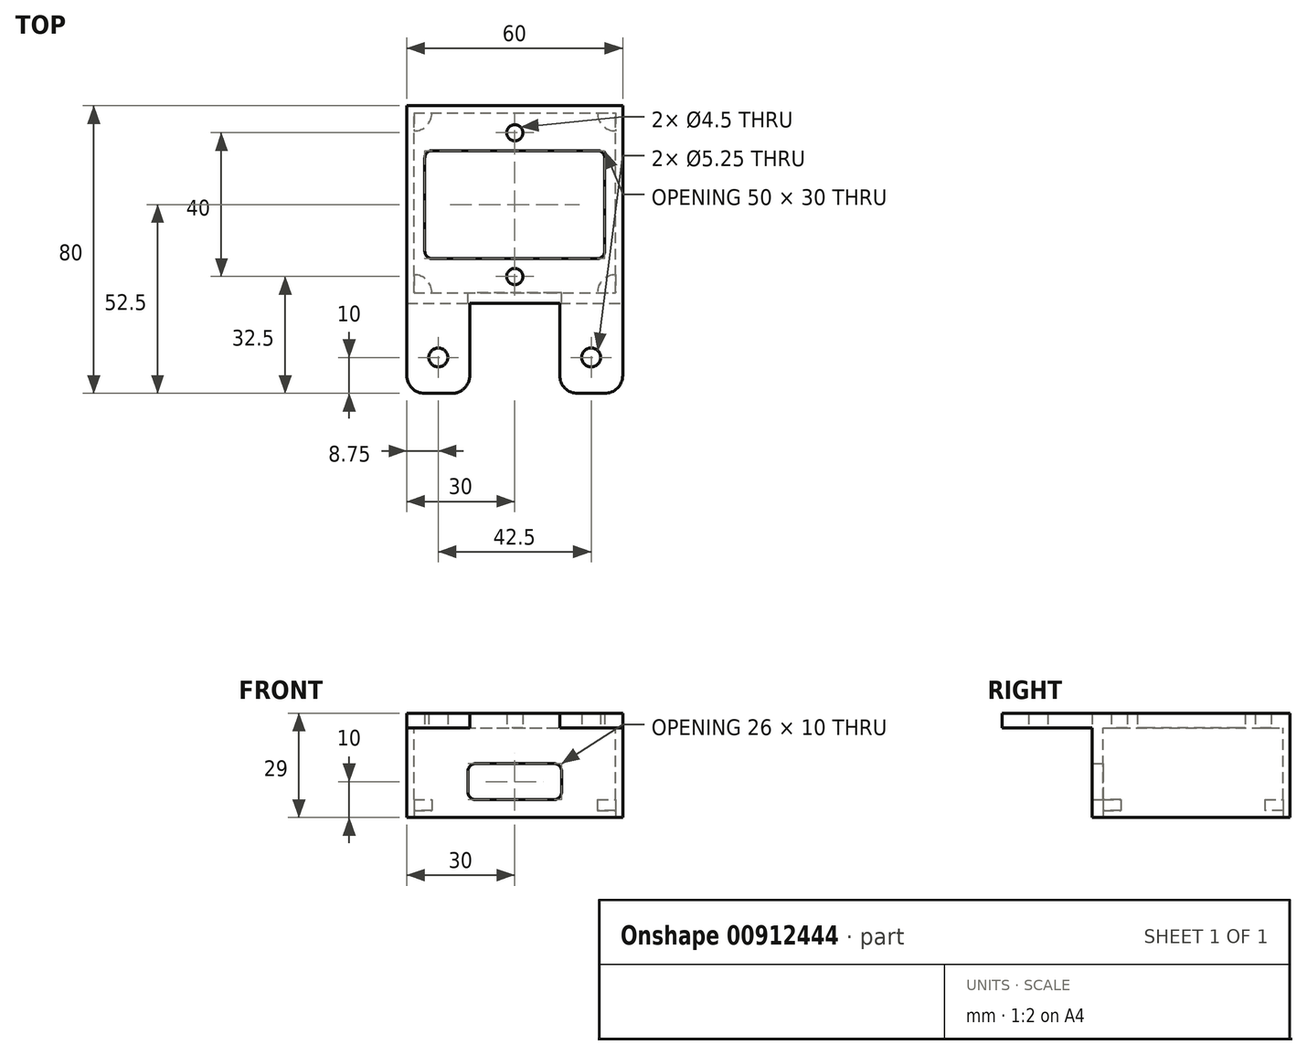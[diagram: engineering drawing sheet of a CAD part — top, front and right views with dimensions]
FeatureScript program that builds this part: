
annotation { "Feature Type Name" : "Feature", "Feature Type Description" : "" }
export const myFeature = defineFeature(function(context is Context, id is Id, definition is map)
    precondition{}
    {
        {
            var Q0;
            Q0=qCreatedBy(makeId("Top.planeOp"),FACE);
            var sketch = newSketch(context, id + "F0", { "sketchPlane" : qUnion([Q0])});
            skLineSegment(sketch, "E0.bottom", {"start": v(-30, 27.5) * mm, "end": v(30, 27.5) * mm});
            skLineSegment(sketch, "E0.left", {"start": v(-30, 27.5) * mm, "end": v(-30, -27.5) * mm});
            skLineSegment(sketch, "E0.right", {"start": v(30, 27.5) * mm, "end": v(30, -27.5) * mm});
            skLineSegment(sketch, "E1.bottom", {"start": v(-23, 15) * mm, "end": v(23, 15) * mm});
            skLineSegment(sketch, "E1.top", {"start": v(-23, -15) * mm, "end": v(23, -15) * mm});
            skLineSegment(sketch, "E1.left", {"start": v(-25, 13) * mm, "end": v(-25, -13) * mm});
            skLineSegment(sketch, "E1.right", {"start": v(25, 13) * mm, "end": v(25, -13) * mm});
            skCircle(sketch, "E2", {"center": v(0, 20) * mm, "radius": 2.25 * mm});
            skCircle(sketch, "E3", {"center": v(0, -20) * mm, "radius": 2.25 * mm});
            skPoint(sketch, "E4.visualSharp", {"position": v(-25, 15) * mm});
            skArc(sketch, "E4.filletArc", {"start": v(-23, 15) * mm, "mid": v(-24.41, 14.41) * mm, "end": v(-25, 13) * mm});
            skPoint(sketch, "E5.visualSharp", {"position": v(-25, -15) * mm});
            skArc(sketch, "E5.filletArc", {"start": v(-25, -13) * mm, "mid": v(-24.41, -14.41) * mm, "end": v(-23, -15) * mm});
            skPoint(sketch, "E6.visualSharp", {"position": v(25, -15) * mm});
            skArc(sketch, "E6.filletArc", {"start": v(23, -15) * mm, "mid": v(24.41, -14.41) * mm, "end": v(25, -13) * mm});
            skPoint(sketch, "E7.visualSharp", {"position": v(25, 15) * mm});
            skArc(sketch, "E7.filletArc", {"start": v(25, 13) * mm, "mid": v(24.41, 14.41) * mm, "end": v(23, 15) * mm});
            skLineSegment(sketch, "E8.top", {"start": v(-25, -52.5) * mm, "end": v(-17.5, -52.5) * mm});
            skLineSegment(sketch, "E8.left", {"start": v(-30, -27.5) * mm, "end": v(-30, -47.5) * mm});
            skLineSegment(sketch, "E9.bottom", {"start": v(30, -27.5) * mm, "end": v(12.5, -27.5) * mm});
            skLineSegment(sketch, "E9.top", {"start": v(25, -52.5) * mm, "end": v(17.5, -52.5) * mm});
            skLineSegment(sketch, "E9.left", {"start": v(30, -27.5) * mm, "end": v(30, -47.5) * mm});
            skLineSegment(sketch, "E9.right", {"start": v(12.5, -27.5) * mm, "end": v(12.5, -47.5) * mm});
            skCircle(sketch, "E10", {"center": v(-21.25, -42.5) * mm, "radius": 2.62 * mm});
            skCircle(sketch, "E11", {"center": v(21.25, -42.5) * mm, "radius": 2.62 * mm});
            skPoint(sketch, "E12.visualSharp", {"position": v(-30, -52.5) * mm});
            skPoint(sketch, "E13.visualSharp", {"position": v(-12.5, -52.5) * mm});
            skPoint(sketch, "E14.visualSharp", {"position": v(12.5, -52.5) * mm});
            skPoint(sketch, "E15.visualSharp", {"position": v(30, -52.5) * mm});
            skArc(sketch, "E15.filletArc", {"start": v(25, -52.5) * mm, "mid": v(28.54, -51.04) * mm, "end": v(30, -47.5) * mm});
            skPoint(sketch, "E16.visualSharp", {"position": v(30, 27.5) * mm});
            skPoint(sketch, "E17.visualSharp", {"position": v(-30, 27.5) * mm});
            skLineSegment(sketch, "E18.filletArc", {"start": v(-30, 27.5) * mm, "end": v(-30, 27.5) * mm});
            skLineSegment(sketch, "E19.filletArc", {"start": v(30, 27.5) * mm, "end": v(30, 27.5) * mm});
            skArc(sketch, "E20.filletArc", {"start": v(-17.5, -52.5) * mm, "mid": v(-13.96, -51.03) * mm, "end": v(-12.5, -47.5) * mm});
            skLineSegment(sketch, "E21", {"start": v(12.5, -27.5) * mm, "end": v(-30, -27.5) * mm});
            skLineSegment(sketch, "E22", {"start": v(-12.5, -47.5) * mm, "end": v(-12.5, -27.5) * mm});
            skArc(sketch, "E23.filletArc", {"start": v(12.5, -47.5) * mm, "mid": v(13.96, -51.04) * mm, "end": v(17.5, -52.5) * mm});
            skArc(sketch, "E24.filletArc", {"start": v(-30, -47.5) * mm, "mid": v(-28.54, -51.04) * mm, "end": v(-25, -52.5) * mm});
            skSolve(sketch);
        }
        {
            var Q0;
            Q0 = qSketchRegion(id + "F0", true);
            extrude(context, id + "F1", {"entities" : qUnion([Q0]), "depth" : 4 * mm, "offsetDistance" : 25 * mm});
        }
        {
            var Q0;
            Q0=makeQuery(id+"F1.opExtrude","CAP_FACE",FACE,{"disambiguationData":[OSD([sQuery(id+"F0.wireOp",EDGE,"E0.bottom"),sQuery(id+"F0.wireOp",EDGE,"E0.left"),sQuery(id+"F0.wireOp",EDGE,"E0.right"),sQuery(id+"F0.wireOp",EDGE,"E1.bottom"),sQuery(id+"F0.wireOp",EDGE,"E1.top"),sQuery(id+"F0.wireOp",EDGE,"E1.left"),sQuery(id+"F0.wireOp",EDGE,"E1.right"),sQuery(id+"F0.wireOp",EDGE,"E2"),sQuery(id+"F0.wireOp",EDGE,"E3"),sQuery(id+"F0.wireOp",EDGE,"E4.filletArc"),sQuery(id+"F0.wireOp",EDGE,"E5.filletArc"),sQuery(id+"F0.wireOp",EDGE,"E6.filletArc"),sQuery(id+"F0.wireOp",EDGE,"E7.filletArc"),sQuery(id+"F0.wireOp",EDGE,"E8.top"),sQuery(id+"F0.wireOp",EDGE,"E8.left"),sQuery(id+"F0.wireOp",EDGE,"E9.top"),sQuery(id+"F0.wireOp",EDGE,"E9.left"),sQuery(id+"F0.wireOp",EDGE,"E9.right"),sQuery(id+"F0.wireOp",EDGE,"E10"),sQuery(id+"F0.wireOp",EDGE,"E11"),sQuery(id+"F0.wireOp",EDGE,"E15.filletArc"),sQuery(id+"F0.wireOp",EDGE,"E18.filletArc"),sQuery(id+"F0.wireOp",EDGE,"E19.filletArc"),sQuery(id+"F0.wireOp",EDGE,"43daff67-91f7-4f9f-9406-6309f67d5902.filletArc"),sQuery(id+"F0.wireOp",EDGE,"E20.filletArc"),sQuery(id+"F0.wireOp",EDGE,"E21"),sQuery(id+"F0.wireOp",EDGE,"E22"),sQuery(id+"F0.wireOp",EDGE,"E23.filletArc")])],"isStart":true});
            var sketch = newSketch(context, id + "F2", { "sketchPlane" : qUnion([Q0])});
            skLineSegment(sketch, "E25.bottom", {"start": v(-30, 27.5) * mm, "end": v(30, 27.5) * mm});
            skLineSegment(sketch, "E25.top", {"start": v(-30, -27.5) * mm, "end": v(30, -27.5) * mm});
            skLineSegment(sketch, "E25.left", {"start": v(-30, 27.5) * mm, "end": v(-30, -27.5) * mm});
            skLineSegment(sketch, "E25.right", {"start": v(30, 27.5) * mm, "end": v(30, -27.5) * mm});
            skLineSegment(sketch, "E26.bottom", {"start": v(-28, 24.5) * mm, "end": v(28, 24.5) * mm});
            skLineSegment(sketch, "E26.top", {"start": v(-28, -25.5) * mm, "end": v(28, -25.5) * mm});
            skLineSegment(sketch, "E26.left", {"start": v(-28, 24.5) * mm, "end": v(-28, -25.5) * mm});
            skLineSegment(sketch, "E26.right", {"start": v(28, 24.5) * mm, "end": v(28, -25.5) * mm});
            skSolve(sketch);
        }
        {
            var Q0;
            Q0 = qSketchRegion(id + "F2", true);
            extrude(context, id + "F3", {"entities" : qUnion([Q0]), "operationType" : NewBodyOperationType.ADD, "depth" : 25 * mm, "offsetDistance" : 25 * mm});
        }
        {
            var Q0;
            Q0=makeQuery(id+"F3.opExtrude","SWEPT_FACE",FACE,{"disambiguationData":[OSD([sQuery(id+"F2.wireOp",EDGE,"E26.bottom")])]});
            var sketch = newSketch(context, id + "F4", { "sketchPlane" : qUnion([Q0])});
            skLineSegment(sketch, "E27.bottom", {"start": v(-11, -10) * mm, "end": v(11, -10) * mm});
            skLineSegment(sketch, "E27.top", {"start": v(-11, -20) * mm, "end": v(11, -20) * mm});
            skLineSegment(sketch, "E27.left", {"start": v(-13, -12) * mm, "end": v(-13, -18) * mm});
            skLineSegment(sketch, "E27.right", {"start": v(13, -12) * mm, "end": v(13, -18) * mm});
            skPoint(sketch, "E28.visualSharp", {"position": v(-13, -10) * mm});
            skArc(sketch, "E28.filletArc", {"start": v(-11, -10) * mm, "mid": v(-12.41, -10.59) * mm, "end": v(-13, -12) * mm});
            skPoint(sketch, "E29.visualSharp", {"position": v(-13, -20) * mm});
            skArc(sketch, "E29.filletArc", {"start": v(-13, -18) * mm, "mid": v(-12.41, -19.41) * mm, "end": v(-11, -20) * mm});
            skPoint(sketch, "E30.visualSharp", {"position": v(13, -20) * mm});
            skArc(sketch, "E30.filletArc", {"start": v(11, -20) * mm, "mid": v(12.41, -19.41) * mm, "end": v(13, -18) * mm});
            skPoint(sketch, "E31.visualSharp", {"position": v(13, -10) * mm});
            skArc(sketch, "E31.filletArc", {"start": v(13, -12) * mm, "mid": v(12.41, -10.59) * mm, "end": v(11, -10) * mm});
            skSolve(sketch);
        }
        {
            var Q0;
            Q0 = qSketchRegion(id + "F4", true);
            extrude(context, id + "F5", {"entities" : qUnion([Q0]), "operationType" : NewBodyOperationType.REMOVE, "oppositeDirection" : true, "depth" : 25 * mm, "offsetDistance" : 25 * mm});
        }
        {
            var Q0;
            Q0=makeQuery(id+"F3.opExtrude","CAP_FACE",FACE,{"disambiguationData":[OSD([sQuery(id+"F2.wireOp",EDGE,"E25.bottom"),sQuery(id+"F2.wireOp",EDGE,"E25.top"),sQuery(id+"F2.wireOp",EDGE,"E25.left"),sQuery(id+"F2.wireOp",EDGE,"E25.right"),sQuery(id+"F2.wireOp",EDGE,"E26.bottom"),sQuery(id+"F2.wireOp",EDGE,"E26.top"),sQuery(id+"F2.wireOp",EDGE,"E26.left"),sQuery(id+"F2.wireOp",EDGE,"E26.right")])],"isStart":false});
            var sketch = newSketch(context, id + "F6", { "sketchPlane" : qUnion([Q0])});
            skLineSegment(sketch, "E32.bottom", {"start": v(-28, 24.5) * mm, "end": v(-23, 24.5) * mm});
            skLineSegment(sketch, "E32.top", {"start": v(-28, 19.5) * mm, "end": v(-23, 19.5) * mm});
            skLineSegment(sketch, "E32.left", {"start": v(-28, 24.5) * mm, "end": v(-28, 19.5) * mm});
            skLineSegment(sketch, "E32.right", {"start": v(-23, 24.5) * mm, "end": v(-23, 19.5) * mm});
            skLineSegment(sketch, "E33.bottom", {"start": v(28, 24.5) * mm, "end": v(23, 24.5) * mm});
            skLineSegment(sketch, "E33.top", {"start": v(28, 19.5) * mm, "end": v(23, 19.5) * mm});
            skLineSegment(sketch, "E33.left", {"start": v(28, 24.5) * mm, "end": v(28, 19.5) * mm});
            skLineSegment(sketch, "E33.right", {"start": v(23, 24.5) * mm, "end": v(23, 19.5) * mm});
            skLineSegment(sketch, "E34.bottom", {"start": v(28, -25.5) * mm, "end": v(23, -25.5) * mm});
            skLineSegment(sketch, "E34.top", {"start": v(28, -20.5) * mm, "end": v(23, -20.5) * mm});
            skLineSegment(sketch, "E34.left", {"start": v(28, -25.5) * mm, "end": v(28, -20.5) * mm});
            skLineSegment(sketch, "E34.right", {"start": v(23, -25.5) * mm, "end": v(23, -20.5) * mm});
            skLineSegment(sketch, "E35.bottom", {"start": v(-28, -25.5) * mm, "end": v(-23, -25.5) * mm});
            skLineSegment(sketch, "E35.top", {"start": v(-28, -20.5) * mm, "end": v(-23, -20.5) * mm});
            skLineSegment(sketch, "E35.left", {"start": v(-28, -25.5) * mm, "end": v(-28, -20.5) * mm});
            skLineSegment(sketch, "E35.right", {"start": v(-23, -25.5) * mm, "end": v(-23, -20.5) * mm});
            skSolve(sketch);
        }
        {
            var Q0;
            Q0 = qSketchRegion(id + "F6", true);
            extrude(context, id + "F7", {"entities" : qUnion([Q0]), "operationType" : NewBodyOperationType.ADD, "oppositeDirection" : true, "depth" : 5 * mm, "offsetDistance" : 25 * mm});
        }
        {
            var Q0;
            Q0=makeQuery(id+"F7.boolean.opBoolean","MERGE",FACE,{"derivedFrom":[makeQuery(id+"F3.opExtrude","CAP_FACE",FACE,{"disambiguationData":[OSD([sQuery(id+"F2.wireOp",EDGE,"E25.bottom"),sQuery(id+"F2.wireOp",EDGE,"E25.top"),sQuery(id+"F2.wireOp",EDGE,"E25.left"),sQuery(id+"F2.wireOp",EDGE,"E25.right"),sQuery(id+"F2.wireOp",EDGE,"E26.bottom"),sQuery(id+"F2.wireOp",EDGE,"E26.top"),sQuery(id+"F2.wireOp",EDGE,"E26.left"),sQuery(id+"F2.wireOp",EDGE,"E26.right")])],"isStart":false}),makeQuery(id+"F7.opExtrude","CAP_FACE",FACE,{"disambiguationData":[OSD([sQuery(id+"F6.wireOp",EDGE,"E32.bottom"),sQuery(id+"F6.wireOp",EDGE,"E32.top"),sQuery(id+"F6.wireOp",EDGE,"E32.left"),sQuery(id+"F6.wireOp",EDGE,"E32.right")])],"isStart":true}),makeQuery(id+"F7.opExtrude","CAP_FACE",FACE,{"disambiguationData":[OSD([sQuery(id+"F6.wireOp",EDGE,"E33.bottom"),sQuery(id+"F6.wireOp",EDGE,"E33.top"),sQuery(id+"F6.wireOp",EDGE,"E33.left"),sQuery(id+"F6.wireOp",EDGE,"E33.right")])],"isStart":true}),makeQuery(id+"F7.opExtrude","CAP_FACE",FACE,{"disambiguationData":[OSD([sQuery(id+"F6.wireOp",EDGE,"E34.bottom"),sQuery(id+"F6.wireOp",EDGE,"E34.top"),sQuery(id+"F6.wireOp",EDGE,"E34.left"),sQuery(id+"F6.wireOp",EDGE,"E34.right")])],"isStart":true}),makeQuery(id+"F7.opExtrude","CAP_FACE",FACE,{"disambiguationData":[OSD([sQuery(id+"F6.wireOp",EDGE,"E35.bottom"),sQuery(id+"F6.wireOp",EDGE,"E35.top"),sQuery(id+"F6.wireOp",EDGE,"E35.left"),sQuery(id+"F6.wireOp",EDGE,"E35.right")])],"isStart":true})]});
            var sketch = newSketch(context, id + "F8", { "sketchPlane" : qUnion([Q0])});
            skLineSegment(sketch, "E36.bottom", {"start": v(-28, -25.5) * mm, "end": v(28, -25.5) * mm});
            skLineSegment(sketch, "E36.top", {"start": v(-28, 24.5) * mm, "end": v(28, 24.5) * mm});
            skLineSegment(sketch, "E36.left", {"start": v(-28, -25.5) * mm, "end": v(-28, 24.5) * mm});
            skLineSegment(sketch, "E36.right", {"start": v(28, -25.5) * mm, "end": v(28, 24.5) * mm});
            skSolve(sketch);
        }
        {
            var Q0;
            Q0 = qSketchRegion(id + "F8", true);
            extrude(context, id + "F9", {"entities" : qUnion([Q0]), "operationType" : NewBodyOperationType.REMOVE, "oppositeDirection" : true, "depth" : 2 * mm, "offsetDistance" : 25 * mm});
        }
        {
            var Q0;
            Q0=makeQuery(id+"F7.opExtrude","SWEPT_EDGE",EDGE,{"disambiguationData":[OSD([sQuery(id+"F6.wireOp",EDGE,"E32.top"),sQuery(id+"F6.wireOp",EDGE,"E32.right")])]});
            var Q1;
            Q1=makeQuery(id+"F7.opExtrude","SWEPT_EDGE",EDGE,{"disambiguationData":[OSD([sQuery(id+"F6.wireOp",EDGE,"E33.top"),sQuery(id+"F6.wireOp",EDGE,"E33.right")])]});
            var Q2;
            Q2=makeQuery(id+"F7.opExtrude","SWEPT_EDGE",EDGE,{"disambiguationData":[OSD([sQuery(id+"F6.wireOp",EDGE,"E34.top"),sQuery(id+"F6.wireOp",EDGE,"E34.right")])]});
            var Q3;
            Q3=makeQuery(id+"F7.opExtrude","SWEPT_EDGE",EDGE,{"disambiguationData":[OSD([sQuery(id+"F6.wireOp",EDGE,"E35.top"),sQuery(id+"F6.wireOp",EDGE,"E35.right")])]});
            fillet(context, id + "F10", {"entities" : qUnion([Q0, Q1, Q2, Q3]), "radius" : 5 * mm, "tangentPropagation" : true, "allowEdgeOverflow" : false});
        }
    });
